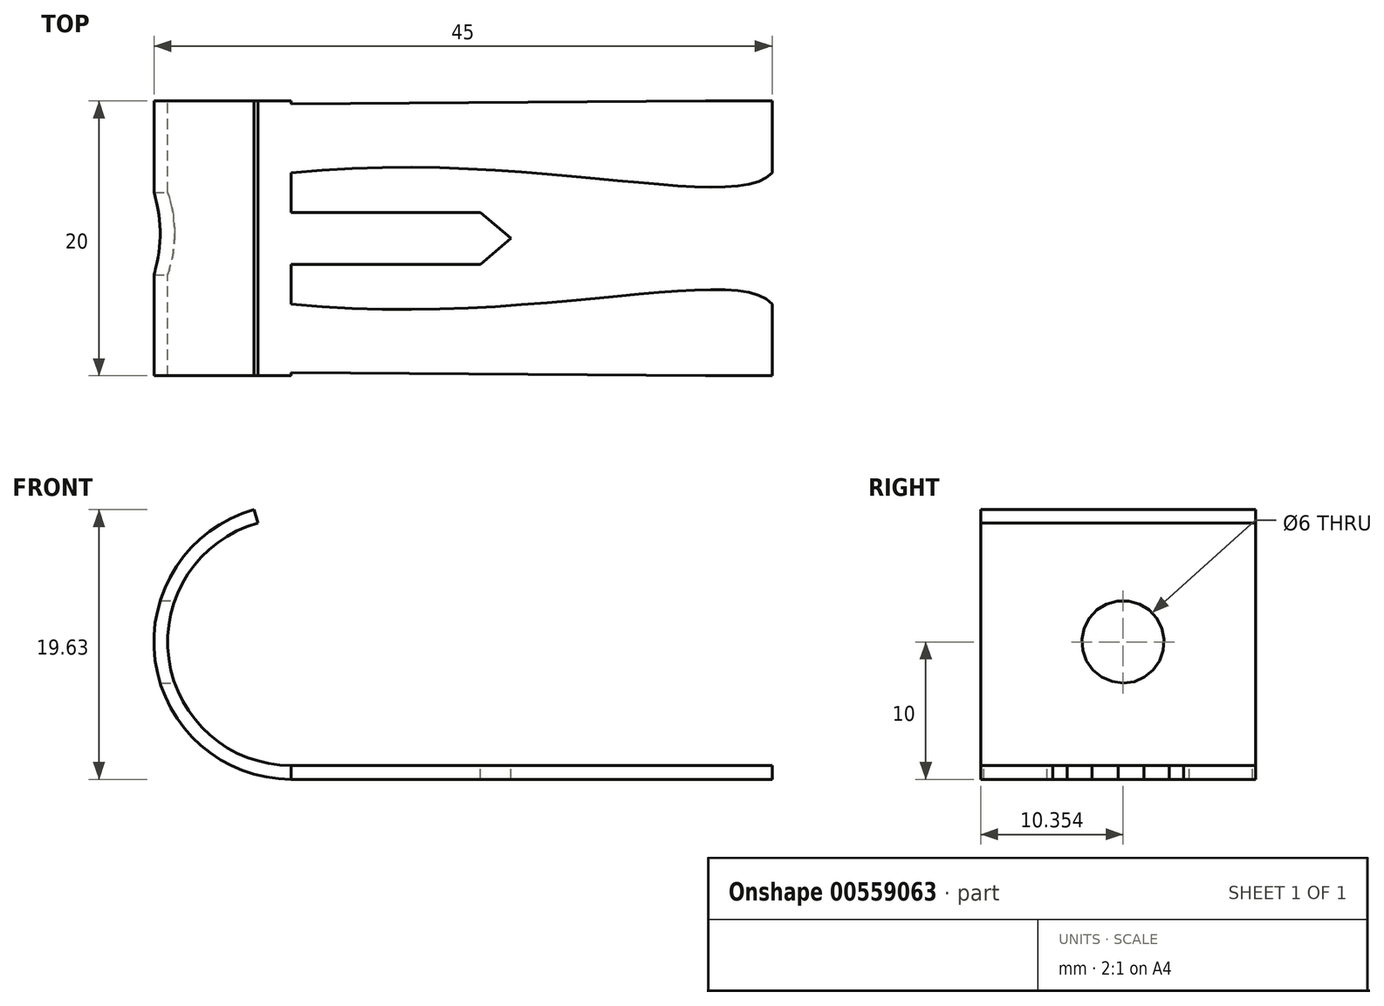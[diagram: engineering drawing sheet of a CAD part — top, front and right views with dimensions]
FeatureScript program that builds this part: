
annotation { "Feature Type Name" : "Feature", "Feature Type Description" : "" }
export const myFeature = defineFeature(function(context is Context, id is Id, definition is map)
    precondition{}
    {
        {
            var Q0;
            Q0=qCreatedBy(makeId("Front.planeOp"),FACE);
            var sketch = newSketch(context, id + "F0", { "sketchPlane" : qUnion([Q0])});
            skCircle(sketch, "E0", {"center": v(0, 0) * mm, "radius": 10 * mm});
            skLineSegment(sketch, "E1.bottom", {"start": v(0, -9) * mm, "end": v(35, -9) * mm});
            skLineSegment(sketch, "E1.top", {"start": v(0, -10) * mm, "end": v(35, -10) * mm});
            skLineSegment(sketch, "E1.left", {"start": v(0, -9) * mm, "end": v(0, -10) * mm});
            skLineSegment(sketch, "E1.right", {"start": v(35, -9) * mm, "end": v(35, -10) * mm});
            skCircle(sketch, "E2", {"center": v(0, 0) * mm, "radius": 9 * mm});
            skLineSegment(sketch, "E3", {"start": v(0, 0) * mm, "end": v(-3.68, 13.15) * mm});
            skLineSegment(sketch, "E4", {"start": v(-3.68, 13.15) * mm, "end": v(10.29, 15.59) * mm});
            skSolve(sketch);
        }
        {
            var Q0;
            {var subQ1=sQuery(id+"F0.wireOp",EDGE,"E1.left");Q0=makeQuery(id+"F0.imprint","IMPRINT",FACE,{"disambiguationData":[TD([[makeQuery(id+"F0.imprint","IMPRINT",EDGE,{"derivedFrom":subQ1}),-1.0]])]});}
            var Q1;
            {var subQ5=sQuery(id+"F0.wireOp",EDGE,"E1.right");Q1=makeQuery(id+"F0.imprint","IMPRINT",FACE,{"disambiguationData":[TD([[makeQuery(id+"F0.imprint","IMPRINT",EDGE,{"derivedFrom":subQ5}),-1.0]])]});}
            var Q2;
            {var subQ5=sQuery(id+"F0.wireOp",EDGE,"E1.left");Q2=makeQuery(id+"F0.imprint","IMPRINT",FACE,{"disambiguationData":[TD([[makeQuery(id+"F0.imprint","IMPRINT",EDGE,{"derivedFrom":subQ5}),1.0]])]});}
            extrude(context, id + "F1", {"entities" : qUnion([Q0, Q1, Q2]), "depth" : 20 * mm, "offsetDistance" : 25 * mm});
        }
        {
            var Q0;
            Q0=makeQuery(id+"F1.opExtrude","SWEPT_FACE",FACE,{"disambiguationData":[OSD([sQuery(id+"F0.wireOp",EDGE,"E1.bottom")])]});
            var sketch = newSketch(context, id + "F2", { "sketchPlane" : qUnion([Q0])});
            skLineSegment(sketch, "E5", {"start": v(-15.67, -10) * mm, "end": v(35.55, -10) * mm});
            skLineSegment(sketch, "E6", {"start": v(35.55, -10) * mm, "end": v(35.55, -9.73) * mm});
            skLineSegment(sketch, "E7", {"start": v(0, -11.89) * mm, "end": v(13.76, -11.89) * mm});
            skLineSegment(sketch, "E8", {"start": v(13.76, -11.89) * mm, "end": v(16, -10) * mm});
            skLineSegment(sketch, "E9", {"start": v(0, -11.89) * mm, "end": v(0, -14.77) * mm});
            skFitSpline(sketch, "E10", {"points": [v(0, -14.77) * mm, v(35, -14.77) * mm, v(30.16, -20) * mm], "startDerivative": vector(75.1, -7.75) * mm, "endDerivative": vector(-46.73, -8.04) * mm});
            skLineSegment(sketch, "E11", {"start": v(30.16, -20) * mm, "end": v(0, -19.78) * mm});
            skLineSegment(sketch, "E12.MirrorCS", {"start": v(13.76, -8.11) * mm, "end": v(16, -10) * mm});
            skLineSegment(sketch, "E13.MirrorCS", {"start": v(0, -8.11) * mm, "end": v(13.76, -8.11) * mm});
            skLineSegment(sketch, "E14.MirrorCS", {"start": v(0, -8.11) * mm, "end": v(0, -5.23) * mm});
            skFitSpline(sketch, "E15.MirrorCS", {"points": [v(0, -5.23) * mm, v(35, -5.23) * mm, v(30.16, 0) * mm], "startDerivative": vector(75.1, 7.75) * mm, "endDerivative": vector(-46.73, 8.04) * mm});
            skLineSegment(sketch, "E16.MirrorCS", {"start": v(30.16, 0) * mm, "end": v(0, -0.22) * mm});
            skLineSegment(sketch, "E17", {"start": v(0, -0.22) * mm, "end": v(0, 0.88) * mm});
            skLineSegment(sketch, "E18", {"start": v(0, -19.78) * mm, "end": v(0, -21.73) * mm});
            skSolve(sketch);
        }
        {
            var Q0;
            {var subQ0=sQuery(id+"F2.wireOp",EDGE,"E16.MirrorCS");Q0=makeQuery(id+"F2.imprint","IMPRINT",FACE,{"disambiguationData":[TD([[makeQuery(id+"F2.imprint","IMPRINT",EDGE,{"derivedFrom":subQ0}),-1.0]])]});}
            var Q1;
            {var subQ0=sQuery(id+"F2.wireOp",EDGE,"E13.MirrorCS");Q1=makeQuery(id+"F2.imprint","IMPRINT",FACE,{"disambiguationData":[TD([[makeQuery(id+"F2.imprint","IMPRINT",EDGE,{"derivedFrom":subQ0}),1.0]])]});}
            var Q2;
            {var subQ2=sQuery(id+"F2.wireOp",EDGE,"E7");Q2=makeQuery(id+"F2.imprint","IMPRINT",FACE,{"disambiguationData":[TD([[makeQuery(id+"F2.imprint","IMPRINT",EDGE,{"derivedFrom":subQ2}),-1.0]])]});}
            var Q3;
            {var subQ0=sQuery(id+"F2.wireOp",EDGE,"E11");Q3=makeQuery(id+"F2.imprint","IMPRINT",FACE,{"disambiguationData":[TD([[makeQuery(id+"F2.imprint","IMPRINT",EDGE,{"derivedFrom":subQ0}),1.0]])]});}
            extrude(context, id + "F3", {"entities" : qUnion([Q0, Q1, Q2, Q3]), "operationType" : NewBodyOperationType.REMOVE, "endBound" : BoundingType.THROUGH_ALL, "oppositeDirection" : true, "depth" : 25 * mm, "offsetDistance" : 25 * mm});
        }
        {
            var Q0;
            Q0=qCreatedBy(makeId("Right.planeOp"),FACE);
            var sketch = newSketch(context, id + "F4", { "sketchPlane" : qUnion([Q0])});
            skLineSegment(sketch, "E19", {"start": v(0, 0) * mm, "end": v(-19.3, 0) * mm});
            skLineSegment(sketch, "E20", {"start": v(-9.65, -4.14) * mm, "end": v(-9.65, 0) * mm});
            skSolve(sketch);
        }
        {
            var Q0;
            Q0=sQuery(id+"F4.wireOp",VERTEX,"E20.end");
            var Q1;
            Q1=makeQuery(id+"F3.boolean.opBoolean","SPLIT",BODY,{"disambiguationData":[OD(0.0)],"derivedFrom":makeQuery(id+"F1.opExtrude","SWEPT_BODY",BODY,{"disambiguationData":[OSD([sQuery(id+"F0.wireOp",EDGE,"E0"),sQuery(id+"F0.wireOp",EDGE,"E1.bottom"),sQuery(id+"F0.wireOp",EDGE,"E1.top"),sQuery(id+"F0.wireOp",EDGE,"E1.right"),sQuery(id+"F0.wireOp",EDGE,"E2"),sQuery(id+"F0.wireOp",EDGE,"E3")])]})});
            hole(context, id + "F5", {"style" : HoleStyle.SIMPLE, "endStyle" : HoleEndStyle.THROUGH, "holeDiameter" : 6 * mm, "isTappedThrough" : true, "tappedDepth" : 12 * mm, "tapClearance" : 3, "locations" : qUnion([Q0]), "scope" : qUnion([Q1])});
        }
    });
